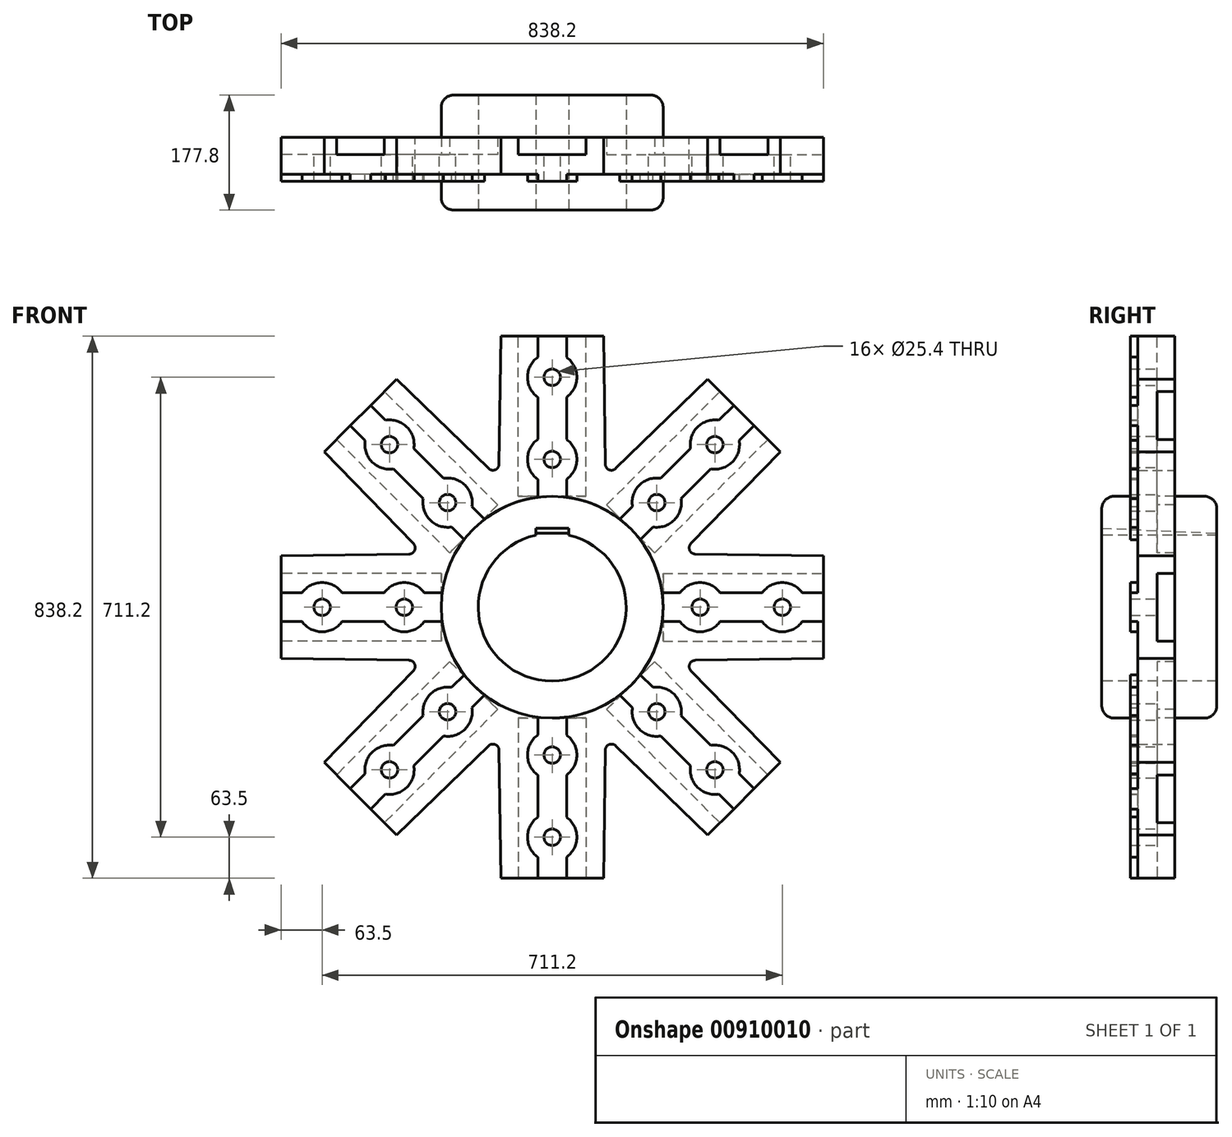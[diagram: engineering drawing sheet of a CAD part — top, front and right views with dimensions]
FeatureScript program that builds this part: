
annotation { "Feature Type Name" : "Feature", "Feature Type Description" : "" }
export const myFeature = defineFeature(function(context is Context, id is Id, definition is map)
    precondition{}
    {
        {
            var Q0;
            Q0=qCreatedBy(makeId("Right.planeOp"),FACE);
            var sketch = newSketch(context, id + "F0", { "sketchPlane" : qUnion([Q0])});
            skLineSegment(sketch, "E0.bottom", {"start": v(-84.14, 171.45) * mm, "end": v(93.66, 171.45) * mm});
            skLineSegment(sketch, "E0.top", {"start": v(-84.14, 114.3) * mm, "end": v(-28.58, 114.3) * mm});
            skLineSegment(sketch, "E0.right", {"start": v(93.66, 171.45) * mm, "end": v(93.66, 114.3) * mm});
            skLineSegment(sketch, "E1", {"start": v(-84.14, 0) * mm, "end": v(93.66, 0) * mm, "construction": true});
            skLineSegment(sketch, "E2", {"start": v(-84.14, 114.3) * mm, "end": v(-84.14, 171.45) * mm});
            skLineSegment(sketch, "E3", {"start": v(-28.58, 114.3) * mm, "end": v(-28.58, 419.1) * mm});
            skLineSegment(sketch, "E4", {"start": v(-28.58, 419.1) * mm, "end": v(28.57, 419.1) * mm});
            skLineSegment(sketch, "E5", {"start": v(28.57, 419.1) * mm, "end": v(28.57, 114.3) * mm});
            skLineSegment(sketch, "E6", {"start": v(0, 419.1) * mm, "end": v(0, 0) * mm, "construction": true});
            skLineSegment(sketch, "E7", {"start": v(-28.58, 114.3) * mm, "end": v(28.58, 114.3) * mm});
            skLineSegment(sketch, "E8", {"start": v(28.58, 114.3) * mm, "end": v(93.66, 114.3) * mm});
            skSolve(sketch);
        }
        {
            var Q0;
            Q0=makeQuery(id+"F0.imprint","IMPRINT",FACE,{"disambiguationData":[TD([[makeQuery(id+"F0.imprint","IMPRINT",EDGE,{"derivedFrom":sQuery(id+"F0.wireOp",EDGE,"E0.bottom")}),-1.0]])]});
            var Q1;
            Q1=sQuery(id+"F0.wireOp",EDGE,"E1");
            revolve(context, id + "F1", {"surfaceOperationType" : NewSurfaceOperationType.NEW, "entities" : qUnion([Q0]), "axis" : qUnion([Q1]), "revolveType" : RevolveType.SYMMETRIC, "angle" : 45 * degree});
        }
        {
            var Q0;
            {var subQ0=makeQuery(id+"F1.opRevolve","SWEPT_EDGE",EDGE,{"disambiguationData":[OSD([sQuery(id+"F0.wireOp",EDGE,"E0.bottom"),sQuery(id+"F0.wireOp",EDGE,"E2")])]});Q0=makeQuery(id+"F10.boolean.opBoolean","MERGE",EDGE,{"derivedFrom":[subQ0,makeQuery(id+"F10.opPattern","COPY",EDGE,{"derivedFrom":subQ0,"instanceName":"1"}),makeQuery(id+"F10.opPattern","COPY",EDGE,{"derivedFrom":subQ0,"instanceName":"2"}),makeQuery(id+"F10.opPattern","COPY",EDGE,{"derivedFrom":subQ0,"instanceName":"3"}),makeQuery(id+"F10.opPattern","COPY",EDGE,{"derivedFrom":subQ0,"instanceName":"4"}),makeQuery(id+"F10.opPattern","COPY",EDGE,{"derivedFrom":subQ0,"instanceName":"5"}),makeQuery(id+"F10.opPattern","COPY",EDGE,{"derivedFrom":subQ0,"instanceName":"6"}),makeQuery(id+"F10.opPattern","COPY",EDGE,{"derivedFrom":subQ0,"instanceName":"7"})]});}
            var Q1;
            {var subQ0=makeQuery(id+"F1.opRevolve","SWEPT_EDGE",EDGE,{"disambiguationData":[OSD([sQuery(id+"F0.wireOp",EDGE,"E0.bottom"),sQuery(id+"F0.wireOp",EDGE,"E0.right")])]});Q1=makeQuery(id+"F10.boolean.opBoolean","MERGE",EDGE,{"derivedFrom":[subQ0,makeQuery(id+"F10.opPattern","COPY",EDGE,{"derivedFrom":subQ0,"instanceName":"1"}),makeQuery(id+"F10.opPattern","COPY",EDGE,{"derivedFrom":subQ0,"instanceName":"2"}),makeQuery(id+"F10.opPattern","COPY",EDGE,{"derivedFrom":subQ0,"instanceName":"3"}),makeQuery(id+"F10.opPattern","COPY",EDGE,{"derivedFrom":subQ0,"instanceName":"4"}),makeQuery(id+"F10.opPattern","COPY",EDGE,{"derivedFrom":subQ0,"instanceName":"5"}),makeQuery(id+"F10.opPattern","COPY",EDGE,{"derivedFrom":subQ0,"instanceName":"6"}),makeQuery(id+"F10.opPattern","COPY",EDGE,{"derivedFrom":subQ0,"instanceName":"7"})]});}
            fillet(context, id + "F2", {"entities" : qUnion([Q0, Q1]), "radius" : 19.05 * mm, "tangentPropagation" : true, "allowEdgeOverflow" : false});
        }
        {
            var Q0;
            {var subQ5=sQuery(id+"F0.wireOp",EDGE,"E7");Q0=makeQuery(id+"F0.imprint","IMPRINT",FACE,{"disambiguationData":[TD([[makeQuery(id+"F0.imprint","IMPRINT",EDGE,{"derivedFrom":subQ5}),1.0]])]});}
            var Q1;
            {var subQ5=sQuery(id+"F0.wireOp",EDGE,"E4");Q1=makeQuery(id+"F0.imprint","IMPRINT",FACE,{"disambiguationData":[TD([[makeQuery(id+"F0.imprint","IMPRINT",EDGE,{"derivedFrom":subQ5}),-1.0]])]});}
            extrude(context, id + "F3", {"entities" : qUnion([Q0, Q1]), "operationType" : NewBodyOperationType.ADD, "depth" : 158.75 * mm, "offsetDistance" : 25 * mm, "symmetric" : true});
        }
        {
            var Q0;
            Q0=makeQuery(id+"F3.opExtrude","SWEPT_FACE",FACE,{"disambiguationData":[OSD([sQuery(id+"F0.wireOp",EDGE,"E3")])]});
            var sketch = newSketch(context, id + "F4", { "sketchPlane" : qUnion([Q0])});
            skLineSegment(sketch, "E9.bottom", {"start": v(-22.23, 170) * mm, "end": v(22.23, 170) * mm});
            skLineSegment(sketch, "E9.top", {"start": v(-22.23, 419.1) * mm, "end": v(22.23, 419.1) * mm});
            skLineSegment(sketch, "E9.left", {"start": v(-22.23, 170) * mm, "end": v(-22.23, 419.1) * mm});
            skLineSegment(sketch, "E9.right", {"start": v(22.22, 170) * mm, "end": v(22.22, 419.1) * mm});
            skCircle(sketch, "E10", {"center": v(0, 355.6) * mm, "radius": 38.1 * mm});
            skCircle(sketch, "E11", {"center": v(0, 228.6) * mm, "radius": 38.1 * mm});
            skCircle(sketch, "E12", {"center": v(0, 355.6) * mm, "radius": 12.7 * mm});
            skCircle(sketch, "E13", {"center": v(0, 228.6) * mm, "radius": 12.7 * mm});
            skLineSegment(sketch, "E14", {"start": v(-79.38, 419.1) * mm, "end": v(-82.55, 190.5) * mm});
            skLineSegment(sketch, "E15", {"start": v(-82.55, 190.5) * mm, "end": v(82.55, 190.5) * mm});
            skLineSegment(sketch, "E16", {"start": v(82.55, 190.5) * mm, "end": v(79.38, 419.1) * mm});
            skSolve(sketch);
        }
        {
            var Q0;
            {var subQ0=sQuery(id+"F4.wireOp",EDGE,"E9.top");Q0=makeQuery(id+"F4.imprint","IMPRINT",FACE,{"disambiguationData":[TD([[makeQuery(id+"F4.imprint","IMPRINT",EDGE,{"derivedFrom":subQ0}),1.0]])]});}
            var Q1;
            {var subQ0=sQuery(id+"F4.wireOp",EDGE,"E10");var subQ1=sQuery(id+"F4.wireOp",EDGE,"E9.left");var subQ2=makeQuery(id+"F4.imprint","INTERSECT",VERTEX,{"disambiguationData":[OD(0.0)],"derivedFrom":[subQ1,subQ0]});Q1=makeQuery(id+"F4.imprint","IMPRINT",FACE,{"disambiguationData":[TD([[makeQuery(id+"F4.imprint","IMPRINT",EDGE,{"disambiguationData":[TD([[subQ2,-1.0]])],"derivedFrom":subQ1}),-1.0]])]});}
            var Q2;
            {var subQ0=sQuery(id+"F4.wireOp",EDGE,"E10");var subQ1=sQuery(id+"F4.wireOp",EDGE,"E9.right");var subQ2=makeQuery(id+"F4.imprint","INTERSECT",VERTEX,{"disambiguationData":[OD(0.0)],"derivedFrom":[subQ1,subQ0]});Q2=makeQuery(id+"F4.imprint","IMPRINT",FACE,{"disambiguationData":[TD([[makeQuery(id+"F4.imprint","IMPRINT",EDGE,{"disambiguationData":[TD([[subQ2,-1.0]])],"derivedFrom":subQ1}),-1.0]])]});}
            var Q3;
            {var subQ0=sQuery(id+"F4.wireOp",EDGE,"E10");var subQ1=sQuery(id+"F4.wireOp",EDGE,"E9.left");var subQ2=makeQuery(id+"F4.imprint","INTERSECT",VERTEX,{"disambiguationData":[OD(0.0)],"derivedFrom":[subQ1,subQ0]});Q3=makeQuery(id+"F4.imprint","IMPRINT",FACE,{"disambiguationData":[TD([[makeQuery(id+"F4.imprint","IMPRINT",EDGE,{"disambiguationData":[TD([[subQ2,-1.0]])],"derivedFrom":subQ1}),1.0]])]});}
            var Q4;
            {var subQ0=sQuery(id+"F4.wireOp",EDGE,"E11");var subQ1=sQuery(id+"F4.wireOp",EDGE,"E9.left");var subQ2=makeQuery(id+"F4.imprint","INTERSECT",VERTEX,{"disambiguationData":[OD(1.0)],"derivedFrom":[subQ1,subQ0]});Q4=makeQuery(id+"F4.imprint","IMPRINT",FACE,{"disambiguationData":[TD([[makeQuery(id+"F4.imprint","IMPRINT",EDGE,{"disambiguationData":[TD([[subQ2,-1.0]])],"derivedFrom":subQ1}),-1.0]])]});}
            var Q5;
            {var subQ0=sQuery(id+"F4.wireOp",EDGE,"E11");var subQ1=sQuery(id+"F4.wireOp",EDGE,"E9.left");var subQ2=makeQuery(id+"F4.imprint","INTERSECT",VERTEX,{"disambiguationData":[OD(0.0)],"derivedFrom":[subQ1,subQ0]});Q5=makeQuery(id+"F4.imprint","IMPRINT",FACE,{"disambiguationData":[TD([[makeQuery(id+"F4.imprint","IMPRINT",EDGE,{"disambiguationData":[TD([[subQ2,-1.0]])],"derivedFrom":subQ1}),-1.0]])]});}
            var Q6;
            {var subQ0=sQuery(id+"F4.wireOp",EDGE,"E11");var subQ1=sQuery(id+"F4.wireOp",EDGE,"E9.left");var subQ2=makeQuery(id+"F4.imprint","INTERSECT",VERTEX,{"disambiguationData":[OD(0.0)],"derivedFrom":[subQ1,subQ0]});Q6=makeQuery(id+"F4.imprint","IMPRINT",FACE,{"disambiguationData":[TD([[makeQuery(id+"F4.imprint","IMPRINT",EDGE,{"disambiguationData":[TD([[subQ2,-1.0]])],"derivedFrom":subQ1}),1.0]])]});}
            var Q7;
            {var subQ0=sQuery(id+"F4.wireOp",EDGE,"E11");var subQ1=sQuery(id+"F4.wireOp",EDGE,"E9.right");var subQ2=makeQuery(id+"F4.imprint","INTERSECT",VERTEX,{"disambiguationData":[OD(0.0)],"derivedFrom":[subQ1,subQ0]});Q7=makeQuery(id+"F4.imprint","IMPRINT",FACE,{"disambiguationData":[TD([[makeQuery(id+"F4.imprint","IMPRINT",EDGE,{"disambiguationData":[TD([[subQ2,-1.0]])],"derivedFrom":subQ1}),-1.0]])]});}
            var Q8;
            {var subQ0=sQuery(id+"F4.wireOp",EDGE,"E9.left");var subQ4=sQuery(id+"F4.wireOp",EDGE,"E11");var subQ5=makeQuery(id+"F4.imprint","INTERSECT",VERTEX,{"disambiguationData":[OD(0.0)],"derivedFrom":[subQ0,subQ4]});Q8=makeQuery(id+"F4.imprint","IMPRINT",FACE,{"disambiguationData":[TD([[makeQuery(id+"F4.imprint","IMPRINT",EDGE,{"disambiguationData":[TD([[subQ5,-1.0]])],"derivedFrom":subQ4}),-1.0]])]});}
            var Q9;
            {var subQ0=sQuery(id+"F4.wireOp",EDGE,"E9.left");var subQ3=sQuery(id+"F4.wireOp",EDGE,"E15");var subQ4=makeQuery(id+"F4.imprint","INTERSECT",VERTEX,{"derivedFrom":[subQ0,subQ3]});Q9=makeQuery(id+"F4.imprint","IMPRINT",FACE,{"disambiguationData":[TD([[makeQuery(id+"F4.imprint","IMPRINT",EDGE,{"disambiguationData":[TD([[subQ4,-1.0]])],"derivedFrom":subQ3}),-1.0]])]});}
            var Q10;
            {var subQ0=sQuery(id+"F4.wireOp",EDGE,"E9.right");var subQ3=sQuery(id+"F4.wireOp",EDGE,"E15");var subQ4=makeQuery(id+"F4.imprint","INTERSECT",VERTEX,{"derivedFrom":[subQ0,subQ3]});Q10=makeQuery(id+"F4.imprint","IMPRINT",FACE,{"disambiguationData":[TD([[makeQuery(id+"F4.imprint","IMPRINT",EDGE,{"disambiguationData":[TD([[subQ4,1.0]])],"derivedFrom":subQ3}),-1.0]])]});}
            var Q11;
            {var subQ0=sQuery(id+"F4.wireOp",EDGE,"E15");var subQ1=sQuery(id+"F4.wireOp",EDGE,"E9.right");var subQ2=makeQuery(id+"F4.imprint","INTERSECT",VERTEX,{"derivedFrom":[subQ1,subQ0]});Q11=makeQuery(id+"F4.imprint","IMPRINT",FACE,{"disambiguationData":[TD([[makeQuery(id+"F4.imprint","IMPRINT",EDGE,{"disambiguationData":[TD([[subQ2,-1.0]])],"derivedFrom":subQ1}),1.0]])]});}
            extrude(context, id + "F5", {"entities" : qUnion([Q0, Q1, Q2, Q3, Q4, Q5, Q6, Q7, Q8, Q9, Q10, Q11]), "operationType" : NewBodyOperationType.ADD, "depth" : 11.1 * mm, "offsetDistance" : 25 * mm});
        }
        {
            var Q0;
            {var subQ0=sQuery(id+"F4.wireOp",EDGE,"E14");Q0=makeQuery(id+"F4.imprint","IMPRINT",FACE,{"disambiguationData":[TD([[makeQuery(id+"F4.imprint","IMPRINT",EDGE,{"derivedFrom":subQ0}),1.0]])]});}
            var Q1;
            {var subQ0=sQuery(id+"F4.wireOp",EDGE,"E16");Q1=makeQuery(id+"F4.imprint","IMPRINT",FACE,{"disambiguationData":[TD([[makeQuery(id+"F4.imprint","IMPRINT",EDGE,{"derivedFrom":subQ0}),1.0]])]});}
            var Q2;
            Q2=makeQuery(id+"F3.opExtrude","SWEPT_FACE",FACE,{"disambiguationData":[OSD([sQuery(id+"F0.wireOp",EDGE,"E5")])]});
            extrude(context, id + "F6", {"entities" : qUnion([Q0, Q1]), "operationType" : NewBodyOperationType.ADD, "endBound" : BoundingType.UP_TO_SURFACE, "oppositeDirection" : true, "depth" : 25 * mm, "endBoundEntityFace" : qUnion([Q2]), "offsetDistance" : 25 * mm});
        }
        {
            var Q0;
            Q0=makeQuery(id+"F4.imprint","IMPRINT",FACE,{"disambiguationData":[TD([[makeQuery(id+"F4.imprint","IMPRINT",EDGE,{"derivedFrom":sQuery(id+"F4.wireOp",EDGE,"E12")}),1.0]])]});
            var Q1;
            Q1=makeQuery(id+"F4.imprint","IMPRINT",FACE,{"disambiguationData":[TD([[makeQuery(id+"F4.imprint","IMPRINT",EDGE,{"derivedFrom":sQuery(id+"F4.wireOp",EDGE,"E13")}),1.0]])]});
            extrude(context, id + "F7", {"entities" : qUnion([Q0, Q1]), "operationType" : NewBodyOperationType.REMOVE, "endBound" : BoundingType.THROUGH_ALL, "oppositeDirection" : true, "depth" : 25 * mm, "offsetDistance" : 25 * mm});
        }
        {
            var Q0;
            Q0=makeQuery(id+"F5.boolean.opBoolean","MERGE",FACE,{"derivedFrom":[makeQuery(id+"F3.opExtrude","SWEPT_FACE",FACE,{"disambiguationData":[OSD([sQuery(id+"F0.wireOp",EDGE,"E4")])]}),makeQuery(id+"F5.opExtrude","SWEPT_FACE",FACE,{"disambiguationData":[OSD([sQuery(id+"F4.wireOp",EDGE,"E9.top")])]})]});
            var sketch = newSketch(context, id + "F8", { "sketchPlane" : qUnion([Q0])});
            skLineSegment(sketch, "E17.bottom", {"start": v(-52.39, 28.57) * mm, "end": v(52.39, 28.57) * mm});
            skLineSegment(sketch, "E17.top", {"start": v(-52.39, 1.59) * mm, "end": v(52.39, 1.59) * mm});
            skLineSegment(sketch, "E17.left", {"start": v(-52.39, 28.57) * mm, "end": v(-52.39, 1.59) * mm});
            skLineSegment(sketch, "E17.right", {"start": v(52.39, 28.57) * mm, "end": v(52.39, 1.59) * mm});
            skLineSegment(sketch, "E18", {"start": v(0, 0) * mm, "end": v(0, 1.59) * mm, "construction": true});
            skSolve(sketch);
        }
        {
            var Q0;
            Q0=makeQuery(id+"F8.imprint","IMPRINT",FACE,{"disambiguationData":[TD([[makeQuery(id+"F8.imprint","IMPRINT",EDGE,{"derivedFrom":sQuery(id+"F8.wireOp",EDGE,"E17.bottom")}),1.0]])]});
            extrude(context, id + "F9", {"entities" : qUnion([Q0]), "operationType" : NewBodyOperationType.REMOVE, "oppositeDirection" : true, "depth" : 247.65 * mm, "offsetDistance" : 25 * mm});
        }
        {
            var Q0;
            Q0=makeQuery(id+"F1.opRevolve","SWEPT_BODY",BODY,{"disambiguationData":[OSD([sQuery(id+"F0.wireOp",EDGE,"E0.bottom"),sQuery(id+"F0.wireOp",EDGE,"E0.top"),sQuery(id+"F0.wireOp",EDGE,"E0.right"),sQuery(id+"F0.wireOp",EDGE,"E2")])]});
            var Q1;
            Q1=sQuery(id+"F0.wireOp",EDGE,"E1");
            circularPattern(context, id + "F10", {"operationType" : NewBodyOperationType.ADD, "entities" : qUnion([Q0]), "axis" : qUnion([Q1]), "angle" : 360 * degree, "instanceCount" : 8, "equalSpace" : true});
        }
        {
            var Q0;
            {var subQ0=sQuery(id+"F0.wireOp",EDGE,"E7");var subQ1=sQuery(id+"F0.wireOp",EDGE,"E5");var subQ2=sQuery(id+"F0.wireOp",EDGE,"E4");var subQ3=sQuery(id+"F0.wireOp",EDGE,"E3");Q0=makeQuery(id+"F10.boolean.opBoolean","INTERSECT",EDGE,{"derivedFrom":[makeQuery(id+"F3.opExtrude","CAP_FACE",FACE,{"disambiguationData":[OSD([subQ3,subQ2,subQ1,subQ0])],"isStart":false}),makeQuery(id+"F10.opPattern","COPY",FACE,{"derivedFrom":makeQuery(id+"F3.opExtrude","CAP_FACE",FACE,{"disambiguationData":[OSD([subQ3,subQ2,subQ1,subQ0])],"isStart":true}),"instanceName":"1"})]});}
            var Q1;
            {var subQ0=sQuery(id+"F0.wireOp",EDGE,"E7");var subQ1=sQuery(id+"F0.wireOp",EDGE,"E5");var subQ2=sQuery(id+"F0.wireOp",EDGE,"E4");var subQ3=sQuery(id+"F0.wireOp",EDGE,"E3");Q1=makeQuery(id+"F10.boolean.opBoolean","INTERSECT",EDGE,{"derivedFrom":[makeQuery(id+"F10.opPattern","COPY",FACE,{"derivedFrom":makeQuery(id+"F3.opExtrude","CAP_FACE",FACE,{"disambiguationData":[OSD([subQ3,subQ2,subQ1,subQ0])],"isStart":false}),"instanceName":"1"}),makeQuery(id+"F10.opPattern","COPY",FACE,{"derivedFrom":makeQuery(id+"F3.opExtrude","CAP_FACE",FACE,{"disambiguationData":[OSD([subQ3,subQ2,subQ1,subQ0])],"isStart":true}),"instanceName":"2"})]});}
            var Q2;
            {var subQ0=sQuery(id+"F0.wireOp",EDGE,"E7");var subQ1=sQuery(id+"F0.wireOp",EDGE,"E5");var subQ2=sQuery(id+"F0.wireOp",EDGE,"E4");var subQ3=sQuery(id+"F0.wireOp",EDGE,"E3");Q2=makeQuery(id+"F10.boolean.opBoolean","INTERSECT",EDGE,{"derivedFrom":[makeQuery(id+"F10.opPattern","COPY",FACE,{"derivedFrom":makeQuery(id+"F3.opExtrude","CAP_FACE",FACE,{"disambiguationData":[OSD([subQ3,subQ2,subQ1,subQ0])],"isStart":false}),"instanceName":"2"}),makeQuery(id+"F10.opPattern","COPY",FACE,{"derivedFrom":makeQuery(id+"F3.opExtrude","CAP_FACE",FACE,{"disambiguationData":[OSD([subQ3,subQ2,subQ1,subQ0])],"isStart":true}),"instanceName":"3"})]});}
            var Q3;
            {var subQ0=sQuery(id+"F0.wireOp",EDGE,"E7");var subQ1=sQuery(id+"F0.wireOp",EDGE,"E5");var subQ2=sQuery(id+"F0.wireOp",EDGE,"E4");var subQ3=sQuery(id+"F0.wireOp",EDGE,"E3");Q3=makeQuery(id+"F10.boolean.opBoolean","INTERSECT",EDGE,{"derivedFrom":[makeQuery(id+"F10.opPattern","COPY",FACE,{"derivedFrom":makeQuery(id+"F3.opExtrude","CAP_FACE",FACE,{"disambiguationData":[OSD([subQ3,subQ2,subQ1,subQ0])],"isStart":false}),"instanceName":"3"}),makeQuery(id+"F10.opPattern","COPY",FACE,{"derivedFrom":makeQuery(id+"F3.opExtrude","CAP_FACE",FACE,{"disambiguationData":[OSD([subQ3,subQ2,subQ1,subQ0])],"isStart":true}),"instanceName":"4"})]});}
            var Q4;
            {var subQ0=sQuery(id+"F0.wireOp",EDGE,"E7");var subQ1=sQuery(id+"F0.wireOp",EDGE,"E5");var subQ2=sQuery(id+"F0.wireOp",EDGE,"E4");var subQ3=sQuery(id+"F0.wireOp",EDGE,"E3");Q4=makeQuery(id+"F10.boolean.opBoolean","INTERSECT",EDGE,{"derivedFrom":[makeQuery(id+"F10.opPattern","COPY",FACE,{"derivedFrom":makeQuery(id+"F3.opExtrude","CAP_FACE",FACE,{"disambiguationData":[OSD([subQ3,subQ2,subQ1,subQ0])],"isStart":false}),"instanceName":"4"}),makeQuery(id+"F10.opPattern","COPY",FACE,{"derivedFrom":makeQuery(id+"F3.opExtrude","CAP_FACE",FACE,{"disambiguationData":[OSD([subQ3,subQ2,subQ1,subQ0])],"isStart":true}),"instanceName":"5"})]});}
            var Q5;
            {var subQ0=sQuery(id+"F0.wireOp",EDGE,"E7");var subQ1=sQuery(id+"F0.wireOp",EDGE,"E5");var subQ2=sQuery(id+"F0.wireOp",EDGE,"E4");var subQ3=sQuery(id+"F0.wireOp",EDGE,"E3");Q5=makeQuery(id+"F10.boolean.opBoolean","INTERSECT",EDGE,{"derivedFrom":[makeQuery(id+"F10.opPattern","COPY",FACE,{"derivedFrom":makeQuery(id+"F3.opExtrude","CAP_FACE",FACE,{"disambiguationData":[OSD([subQ3,subQ2,subQ1,subQ0])],"isStart":false}),"instanceName":"5"}),makeQuery(id+"F10.opPattern","COPY",FACE,{"derivedFrom":makeQuery(id+"F3.opExtrude","CAP_FACE",FACE,{"disambiguationData":[OSD([subQ3,subQ2,subQ1,subQ0])],"isStart":true}),"instanceName":"6"})]});}
            var Q6;
            {var subQ0=sQuery(id+"F0.wireOp",EDGE,"E7");var subQ1=sQuery(id+"F0.wireOp",EDGE,"E5");var subQ2=sQuery(id+"F0.wireOp",EDGE,"E4");var subQ3=sQuery(id+"F0.wireOp",EDGE,"E3");Q6=makeQuery(id+"F10.boolean.opBoolean","INTERSECT",EDGE,{"derivedFrom":[makeQuery(id+"F10.opPattern","COPY",FACE,{"derivedFrom":makeQuery(id+"F3.opExtrude","CAP_FACE",FACE,{"disambiguationData":[OSD([subQ3,subQ2,subQ1,subQ0])],"isStart":false}),"instanceName":"6"}),makeQuery(id+"F10.opPattern","COPY",FACE,{"derivedFrom":makeQuery(id+"F3.opExtrude","CAP_FACE",FACE,{"disambiguationData":[OSD([subQ3,subQ2,subQ1,subQ0])],"isStart":true}),"instanceName":"7"})]});}
            var Q7;
            {var subQ0=sQuery(id+"F0.wireOp",EDGE,"E7");var subQ1=sQuery(id+"F0.wireOp",EDGE,"E5");var subQ2=sQuery(id+"F0.wireOp",EDGE,"E4");var subQ3=sQuery(id+"F0.wireOp",EDGE,"E3");Q7=makeQuery(id+"F10.boolean.opBoolean","INTERSECT",EDGE,{"derivedFrom":[makeQuery(id+"F3.opExtrude","CAP_FACE",FACE,{"disambiguationData":[OSD([subQ3,subQ2,subQ1,subQ0])],"isStart":true}),makeQuery(id+"F10.opPattern","COPY",FACE,{"derivedFrom":makeQuery(id+"F3.opExtrude","CAP_FACE",FACE,{"disambiguationData":[OSD([subQ3,subQ2,subQ1,subQ0])],"isStart":false}),"instanceName":"7"})]});}
            var Q8;
            Q8=makeQuery(id+"F10.boolean.opBoolean","INTERSECT",EDGE,{"derivedFrom":[makeQuery(id+"F6.opExtrude","SWEPT_FACE",FACE,{"disambiguationData":[OSD([sQuery(id+"F4.wireOp",EDGE,"E14")])]}),makeQuery(id+"F10.opPattern","COPY",FACE,{"derivedFrom":makeQuery(id+"F6.opExtrude","SWEPT_FACE",FACE,{"disambiguationData":[OSD([sQuery(id+"F4.wireOp",EDGE,"E16")])]}),"instanceName":"7"})]});
            var Q9;
            Q9=makeQuery(id+"F10.boolean.opBoolean","INTERSECT",EDGE,{"derivedFrom":[makeQuery(id+"F6.opExtrude","SWEPT_FACE",FACE,{"disambiguationData":[OSD([sQuery(id+"F4.wireOp",EDGE,"E16")])]}),makeQuery(id+"F10.opPattern","COPY",FACE,{"derivedFrom":makeQuery(id+"F6.opExtrude","SWEPT_FACE",FACE,{"disambiguationData":[OSD([sQuery(id+"F4.wireOp",EDGE,"E14")])]}),"instanceName":"1"})]});
            var Q10;
            Q10=makeQuery(id+"F10.boolean.opBoolean","INTERSECT",EDGE,{"derivedFrom":[makeQuery(id+"F10.opPattern","COPY",FACE,{"derivedFrom":makeQuery(id+"F6.opExtrude","SWEPT_FACE",FACE,{"disambiguationData":[OSD([sQuery(id+"F4.wireOp",EDGE,"E16")])]}),"instanceName":"1"}),makeQuery(id+"F10.opPattern","COPY",FACE,{"derivedFrom":makeQuery(id+"F6.opExtrude","SWEPT_FACE",FACE,{"disambiguationData":[OSD([sQuery(id+"F4.wireOp",EDGE,"E14")])]}),"instanceName":"2"})]});
            var Q11;
            Q11=makeQuery(id+"F10.boolean.opBoolean","INTERSECT",EDGE,{"derivedFrom":[makeQuery(id+"F10.opPattern","COPY",FACE,{"derivedFrom":makeQuery(id+"F6.opExtrude","SWEPT_FACE",FACE,{"disambiguationData":[OSD([sQuery(id+"F4.wireOp",EDGE,"E16")])]}),"instanceName":"2"}),makeQuery(id+"F10.opPattern","COPY",FACE,{"derivedFrom":makeQuery(id+"F6.opExtrude","SWEPT_FACE",FACE,{"disambiguationData":[OSD([sQuery(id+"F4.wireOp",EDGE,"E14")])]}),"instanceName":"3"})]});
            var Q12;
            Q12=makeQuery(id+"F10.boolean.opBoolean","INTERSECT",EDGE,{"derivedFrom":[makeQuery(id+"F10.opPattern","COPY",FACE,{"derivedFrom":makeQuery(id+"F6.opExtrude","SWEPT_FACE",FACE,{"disambiguationData":[OSD([sQuery(id+"F4.wireOp",EDGE,"E16")])]}),"instanceName":"3"}),makeQuery(id+"F10.opPattern","COPY",FACE,{"derivedFrom":makeQuery(id+"F6.opExtrude","SWEPT_FACE",FACE,{"disambiguationData":[OSD([sQuery(id+"F4.wireOp",EDGE,"E14")])]}),"instanceName":"4"})]});
            var Q13;
            Q13=makeQuery(id+"F10.boolean.opBoolean","INTERSECT",EDGE,{"derivedFrom":[makeQuery(id+"F10.opPattern","COPY",FACE,{"derivedFrom":makeQuery(id+"F6.opExtrude","SWEPT_FACE",FACE,{"disambiguationData":[OSD([sQuery(id+"F4.wireOp",EDGE,"E16")])]}),"instanceName":"4"}),makeQuery(id+"F10.opPattern","COPY",FACE,{"derivedFrom":makeQuery(id+"F6.opExtrude","SWEPT_FACE",FACE,{"disambiguationData":[OSD([sQuery(id+"F4.wireOp",EDGE,"E14")])]}),"instanceName":"5"})]});
            var Q14;
            Q14=makeQuery(id+"F10.boolean.opBoolean","INTERSECT",EDGE,{"derivedFrom":[makeQuery(id+"F10.opPattern","COPY",FACE,{"derivedFrom":makeQuery(id+"F6.opExtrude","SWEPT_FACE",FACE,{"disambiguationData":[OSD([sQuery(id+"F4.wireOp",EDGE,"E16")])]}),"instanceName":"5"}),makeQuery(id+"F10.opPattern","COPY",FACE,{"derivedFrom":makeQuery(id+"F6.opExtrude","SWEPT_FACE",FACE,{"disambiguationData":[OSD([sQuery(id+"F4.wireOp",EDGE,"E14")])]}),"instanceName":"6"})]});
            var Q15;
            Q15=makeQuery(id+"F10.boolean.opBoolean","INTERSECT",EDGE,{"derivedFrom":[makeQuery(id+"F10.opPattern","COPY",FACE,{"derivedFrom":makeQuery(id+"F6.opExtrude","SWEPT_FACE",FACE,{"disambiguationData":[OSD([sQuery(id+"F4.wireOp",EDGE,"E16")])]}),"instanceName":"6"}),makeQuery(id+"F10.opPattern","COPY",FACE,{"derivedFrom":makeQuery(id+"F6.opExtrude","SWEPT_FACE",FACE,{"disambiguationData":[OSD([sQuery(id+"F4.wireOp",EDGE,"E14")])]}),"instanceName":"7"})]});
            fillet(context, id + "F11", {"entities" : qUnion([Q0, Q1, Q2, Q3, Q4, Q5, Q6, Q7, Q8, Q9, Q10, Q11, Q12, Q13, Q14, Q15]), "radius" : 9.53 * mm, "tangentPropagation" : true, "allowEdgeOverflow" : false});
        }
        {
            var Q0;
            Q0=qCreatedBy(makeId("Right.planeOp"),FACE);
            var sketch = newSketch(context, id + "F12", { "sketchPlane" : qUnion([Q0])});
            skLineSegment(sketch, "E19", {"start": v(93.66, 0) * mm, "end": v(-84.14, 0) * mm});
            skLineSegment(sketch, "E20", {"start": v(-84.14, 0) * mm, "end": v(-84.14, 122.06) * mm});
            skLineSegment(sketch, "E21", {"start": v(-84.14, 122.06) * mm, "end": v(93.66, 114.3) * mm});
            skLineSegment(sketch, "E22", {"start": v(93.66, 114.3) * mm, "end": v(93.66, 0) * mm});
            skSolve(sketch);
        }
        {
            var Q0;
            Q0=makeQuery(id+"F12.imprint","IMPRINT",FACE,{"disambiguationData":[TD([[makeQuery(id+"F12.imprint","IMPRINT",EDGE,{"derivedFrom":sQuery(id+"F12.wireOp",EDGE,"E19")}),-1.0]])]});
            extrude(context, id + "F13", {"entities" : qUnion([Q0]), "operationType" : NewBodyOperationType.REMOVE, "oppositeDirection" : true, "depth" : 50.8 * mm, "offsetDistance" : 25 * mm, "symmetric" : true});
        }
    });
